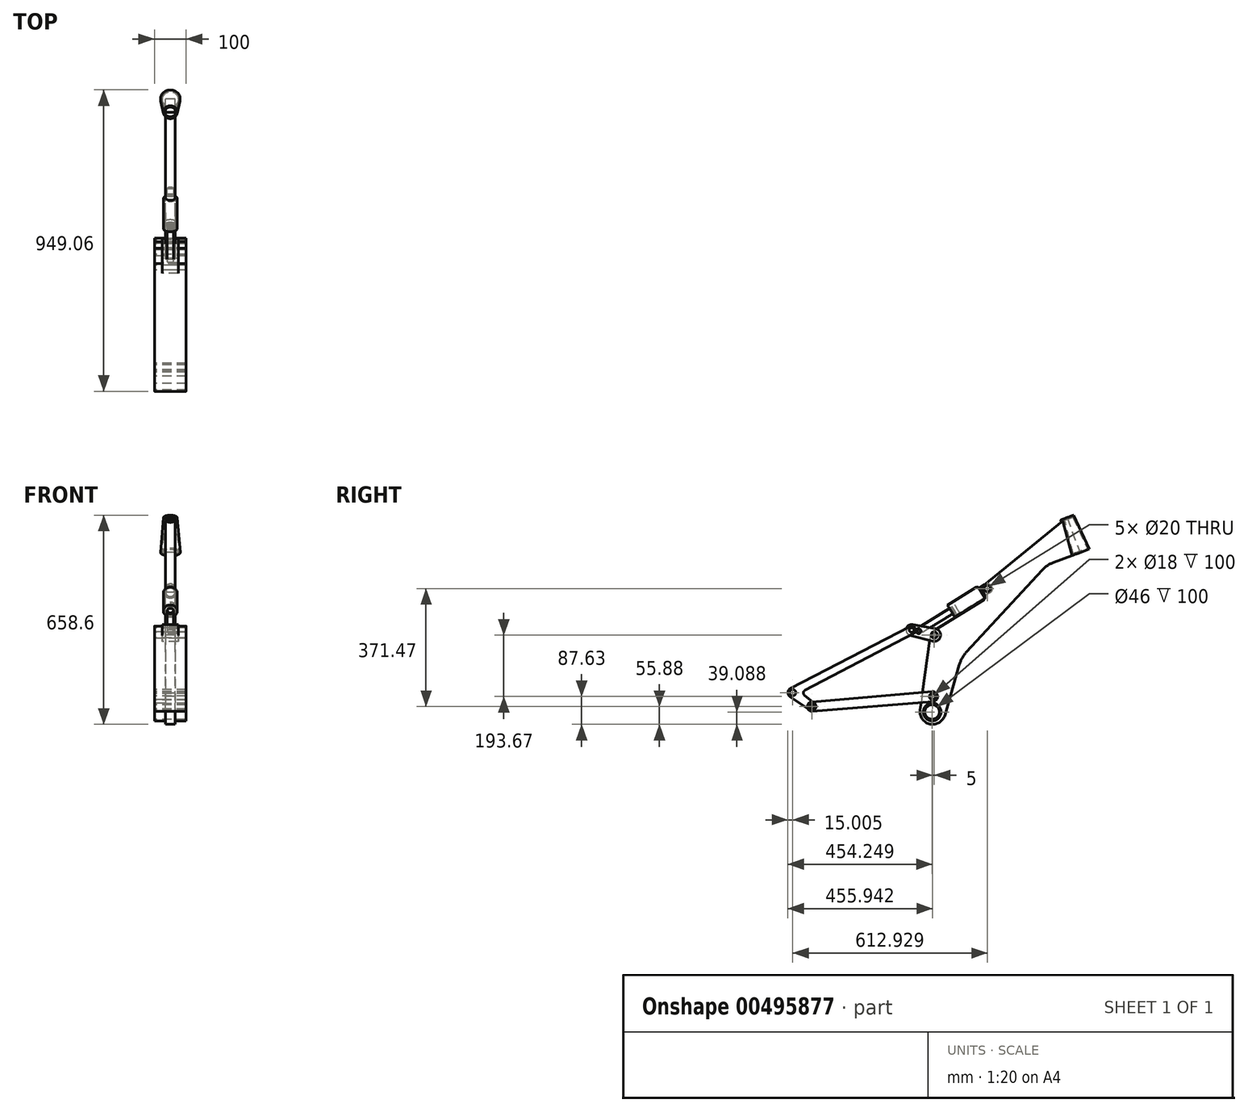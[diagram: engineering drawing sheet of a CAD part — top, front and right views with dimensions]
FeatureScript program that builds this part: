
annotation { "Feature Type Name" : "Feature", "Feature Type Description" : "" }
export const myFeature = defineFeature(function(context is Context, id is Id, definition is map)
    precondition{}
    {
        {
            var Q0;
            Q0=qCreatedBy(makeId("Right.planeOp"),FACE);
            var sketch = newSketch(context, id + "F0", { "sketchPlane" : qUnion([Q0])});
            skLineSegment(sketch, "E0", {"start": v(0, 0) * mm, "end": v(-83.68, 223.8) * mm, "construction": true});
            skLineSegment(sketch, "E1", {"start": v(-295.85, 645.65) * mm, "end": v(-16.13, -102.49) * mm, "construction": true});
            skPoint(sketch, "E2", {"position": v(-219.37, 441.1) * mm});
            skLineSegment(sketch, "E3", {"start": v(-285.85, 416.25) * mm, "end": v(-152.9, 465.96) * mm, "construction": true});
            skCircle(sketch, "E4", {"center": v(0, -8.13) * mm, "radius": 375.7 * mm, "construction": true});
            skPoint(sketch, "E5", {"position": v(-260.46, 551) * mm});
            skPoint(sketch, "E6", {"position": v(-683.46, -60) * mm});
            skPoint(sketch, "E7", {"position": v(-1124.4, 0) * mm});
            skLineSegment(sketch, "E8", {"start": v(-1124.4, 0) * mm, "end": v(0, 0) * mm, "construction": true});
            skCircle(sketch, "E9", {"center": v(-1124.4, 0) * mm, "radius": 375.7 * mm, "construction": true});
            skLineSegment(sketch, "E10", {"start": v(-683.46, -60) * mm, "end": v(-904.4, 662.68) * mm, "construction": true});
            skLineSegment(sketch, "E11", {"start": v(-260.46, 551) * mm, "end": v(-947.84, 551) * mm, "construction": true});
            skPoint(sketch, "E12", {"position": v(-870.26, 551) * mm});
            skLineSegment(sketch, "E13", {"start": v(-207.61, 570.76) * mm, "end": v(-313.3, 531.24) * mm, "construction": true});
            skPoint(sketch, "E14", {"position": v(-249.95, 522.9) * mm});
            skLineSegment(sketch, "E15", {"start": v(-683.46, -60) * mm, "end": v(-249.95, 522.9) * mm, "construction": true});
            skPoint(sketch, "E16", {"position": v(-785.79, 274.7) * mm});
            skLineSegment(sketch, "E17", {"start": v(-785.79, 274.7) * mm, "end": v(-249.95, 522.9) * mm, "construction": true});
            skPoint(sketch, "E18", {"position": v(-466.7, 231.45) * mm});
            skPoint(sketch, "E19", {"position": v(-517.87, 398.8) * mm});
            skSolve(sketch);
        }
        {
            var Q0;
            Q0=qCreatedBy(makeId("Right.planeOp"),FACE);
            var sketch = newSketch(context, id + "F1", { "sketchPlane" : qUnion([Q0])});
            skLineSegment(sketch, "E20", {"start": v(-243.73, 432) * mm, "end": v(-245.48, 436.69) * mm});
            skLineSegment(sketch, "E21", {"start": v(-275.1, 540.19) * mm, "end": v(-245.48, 436.69) * mm});
            skLineSegment(sketch, "E22", {"start": v(-275.1, 540.19) * mm, "end": v(-276.85, 544.87) * mm});
            skLineSegment(sketch, "E23", {"start": v(-276.85, 544.87) * mm, "end": v(-280.8, 543.4) * mm});
            skLineSegment(sketch, "E24", {"start": v(-280.8, 543.4) * mm, "end": v(-248.4, 430.25) * mm});
            skLineSegment(sketch, "E25", {"start": v(-248.4, 430.25) * mm, "end": v(-243.73, 432) * mm});
            skSolve(sketch);
        }
        {
            var Q0;
            Q0=qSketchRegion(id+"F1",true);
            var Q1;
            Q1=sQuery(id+"F0.wireOp",EDGE,"E1");
            revolve(context, id + "F2", {"entities" : qUnion([Q0]), "axis" : qUnion([Q1]), "revolveType" : RevolveType.FULL});
        }
        {
            var Q0;
            Q0=qCreatedBy(makeId("Right.planeOp"),FACE);
            var sketch = newSketch(context, id + "F3", { "sketchPlane" : qUnion([Q0])});
            skCircle(sketch, "E26", {"center": v(-685.15, -60.91) * mm, "radius": 23 * mm});
            skCircle(sketch, "E27", {"center": v(-685.15, -60.91) * mm, "radius": 28 * mm});
            skSolve(sketch);
        }
        {
            var Q0;
            Q0=qSketchRegion(id+"F3",true);
            extrude(context, id + "F4", {"entities" : qUnion([Q0]), "operationType" : NewBodyOperationType.ADD, "endBound" : BoundingType.SYMMETRIC, "depth" : 100 * mm});
        }
        {
            var Q0;
            Q0=qCreatedBy(makeId("Right.planeOp"),FACE);
            var sketch = newSketch(context, id + "F5", { "sketchPlane" : qUnion([Q0])});
            skPoint(sketch, "E28", {"position": v(-683.46, -12.37) * mm});
            skPoint(sketch, "E29", {"position": v(-1063.13, -44.12) * mm});
            skPoint(sketch, "E30", {"position": v(-678.46, 181.3) * mm});
            skPoint(sketch, "E31", {"position": v(-727.65, 194) * mm});
            skPoint(sketch, "E32", {"position": v(-511.47, 327.35) * mm});
            skPoint(sketch, "E33", {"position": v(-749.65, 197.18) * mm});
            skSolve(sketch);
        }
        {
            var Q0;
            Q0=qCreatedBy(makeId("Right.planeOp"),FACE);
            var sketch = newSketch(context, id + "F6", { "sketchPlane" : qUnion([Q0])});
            skArc(sketch, "E34", {"start": v(-520.93, 338.98) * mm, "mid": v(-525.9, 331.46) * mm, "end": v(-525.64, 322.45) * mm});
            skArc(sketch, "E35", {"start": v(-685, 191.95) * mm, "mid": v(-689.37, 187.4) * mm, "end": v(-690.96, 181.3) * mm});
            skLineSegment(sketch, "E36", {"start": v(-690.96, 181.3) * mm, "end": v(-723.1, -54.6) * mm});
            skLineSegment(sketch, "E37", {"start": v(-520.93, 338.98) * mm, "end": v(-260.46, 551) * mm});
            skArc(sketch, "E38", {"start": v(-723.1, -54.6) * mm, "mid": v(-691.69, -99.14) * mm, "end": v(-645, -71.01) * mm});
            skLineSegment(sketch, "E39", {"start": v(-645, -71.01) * mm, "end": v(-599.6, 87.53) * mm});
            skLineSegment(sketch, "E40", {"start": v(-576.93, 127.84) * mm, "end": v(-338.3, 386.26) * mm});
            skLineSegment(sketch, "E41", {"start": v(-303.46, 409.67) * mm, "end": v(-219.37, 441.1) * mm});
            skLineSegment(sketch, "E42", {"start": v(-260.46, 551) * mm, "end": v(-219.37, 441.1) * mm});
            skArc(sketch, "E43", {"start": v(-303.46, 409.67) * mm, "mid": v(-322.26, 400.01) * mm, "end": v(-338.3, 386.26) * mm});
            skCircle(sketch, "E44", {"center": v(-683.46, -12.28) * mm, "radius": 10 * mm});
            skArc(sketch, "E45", {"start": v(-576.93, 127.84) * mm, "mid": v(-590.62, 109.02) * mm, "end": v(-599.6, 87.53) * mm});
            skCircle(sketch, "E46", {"center": v(-678.46, 181.3) * mm, "radius": 10 * mm});
            skCircle(sketch, "E47", {"center": v(-511.47, 327.35) * mm, "radius": 10 * mm});
            skLineSegment(sketch, "E48", {"start": v(-685, 191.95) * mm, "end": v(-523.22, 291.48) * mm});
            skArc(sketch, "E49", {"start": v(-523.22, 291.48) * mm, "mid": v(-519.04, 296.64) * mm, "end": v(-519, 303.27) * mm});
            skLineSegment(sketch, "E50", {"start": v(-525.64, 322.45) * mm, "end": v(-519, 303.27) * mm});
            skCircle(sketch, "E51", {"center": v(-685.15, -60.91) * mm, "radius": 28 * mm});
            skSolve(sketch);
        }
        {
            var Q0;
            Q0 = qSketchRegion(id + "F6", true);
            extrude(context, id + "F7", {"entities" : qUnion([Q0]), "operationType" : NewBodyOperationType.ADD, "endBound" : BoundingType.SYMMETRIC, "depth" : 30 * mm});
        }
        {
            var Q0;
            Q0=qCreatedBy(makeId("Right.planeOp"),FACE);
            var sketch = newSketch(context, id + "F8", { "sketchPlane" : qUnion([Q0])});
            skCircle(sketch, "E52", {"center": v(-683.46, -12.37) * mm, "radius": 10 * mm});
            skCircle(sketch, "E53", {"center": v(-683.46, -12.37) * mm, "radius": 9 * mm});
            skSolve(sketch);
        }
        {
            var Q0;
            Q0 = qSketchRegion(id + "F8", true);
            extrude(context, id + "F9", {"entities" : qUnion([Q0]), "operationType" : NewBodyOperationType.ADD, "endBound" : BoundingType.SYMMETRIC, "depth" : 100 * mm});
        }
        {
            var Q0;
            Q0=qCreatedBy(makeId("Right.planeOp"),FACE);
            var sketch = newSketch(context, id + "F10", { "sketchPlane" : qUnion([Q0])});
            skCircle(sketch, "E54", {"center": v(-678.46, 181.3) * mm, "radius": 10 * mm});
            skCircle(sketch, "E55", {"center": v(-678.46, 181.3) * mm, "radius": 9 * mm});
            skSolve(sketch);
        }
        {
            var Q0;
            Q0 = qSketchRegion(id + "F10", true);
            extrude(context, id + "F11", {"entities" : qUnion([Q0]), "operationType" : NewBodyOperationType.ADD, "endBound" : BoundingType.SYMMETRIC, "depth" : 100 * mm});
        }
        {
            var Q0;
            Q0=qCreatedBy(makeId("Right.planeOp"),FACE);
            var sketch = newSketch(context, id + "F12", { "sketchPlane" : qUnion([Q0])});
            skCircle(sketch, "E56", {"center": v(-511.47, 327.35) * mm, "radius": 10 * mm});
            skCircle(sketch, "E57", {"center": v(-511.47, 327.35) * mm, "radius": 9 * mm});
            skSolve(sketch);
        }
        {
            var Q0;
            Q0 = qSketchRegion(id + "F12", true);
            extrude(context, id + "F13", {"entities" : qUnion([Q0]), "operationType" : NewBodyOperationType.ADD, "endBound" : BoundingType.SYMMETRIC, "depth" : 100 * mm});
        }
        {
            var Q0;
            Q0=qCreatedBy(makeId("Right.planeOp"),FACE);
            var sketch = newSketch(context, id + "F14", { "sketchPlane" : qUnion([Q0])});
            skLineSegment(sketch, "E58", {"start": v(-1064.4, -29.17) * mm, "end": v(-684.77, 3.07) * mm});
            skLineSegment(sketch, "E59", {"start": v(-1061.9, -59.07) * mm, "end": v(-682.19, -27.82) * mm});
            skArc(sketch, "E60", {"start": v(-682.19, -27.82) * mm, "mid": v(-668.01, -11.08) * mm, "end": v(-684.77, 3.07) * mm});
            skArc(sketch, "E61", {"start": v(-1064.4, -29.17) * mm, "mid": v(-1078.08, -45.37) * mm, "end": v(-1061.9, -59.07) * mm});
            skCircle(sketch, "E62", {"center": v(-683.46, -12.37) * mm, "radius": 10.5 * mm});
            skCircle(sketch, "E63", {"center": v(-1063.13, -44.12) * mm, "radius": 10 * mm});
            skSolve(sketch);
        }
        {
            var Q0;
            Q0 = qSketchRegion(id + "F14", true);
            extrude(context, id + "F15", {"entities" : qUnion([Q0]), "endBound" : BoundingType.SYMMETRIC, "depth" : 100 * mm});
        }
        {
            var Q0;
            Q0=qCreatedBy(makeId("Right.planeOp"),FACE);
            var sketch = newSketch(context, id + "F16", { "sketchPlane" : qUnion([Q0])});
            skLineSegment(sketch, "E64", {"start": v(-746.42, 214.38) * mm, "end": v(-674.78, 200.96) * mm});
            skLineSegment(sketch, "E65", {"start": v(-754.04, 180.24) * mm, "end": v(-683.48, 161.94) * mm});
            skArc(sketch, "E66", {"start": v(-746.42, 214.38) * mm, "mid": v(-766.73, 201) * mm, "end": v(-754.04, 180.24) * mm});
            skArc(sketch, "E67", {"start": v(-683.48, 161.94) * mm, "mid": v(-658.94, 176.95) * mm, "end": v(-674.78, 200.96) * mm});
            skCircle(sketch, "E68", {"center": v(-749.65, 197.18) * mm, "radius": 7.5 * mm});
            skCircle(sketch, "E69", {"center": v(-678.46, 181.3) * mm, "radius": 10 * mm});
            skCircle(sketch, "E70", {"center": v(-727.65, 194) * mm, "radius": 7.5 * mm});
            skSolve(sketch);
        }
        {
            var Q0;
            Q0 = qSketchRegion(id + "F16", true);
            extrude(context, id + "F17", {"entities" : qUnion([Q0]), "endBound" : BoundingType.SYMMETRIC, "depth" : 50 * mm});
        }
        {
            var Q0;
            Q0=qCreatedBy(makeId("Right.planeOp"),FACE);
            var sketch = newSketch(context, id + "F18", { "sketchPlane" : qUnion([Q0])});
            skLineSegment(sketch, "E71", {"start": v(-1055.2, -34.46) * mm, "end": v(-1087.68, -7.78) * mm});
            skLineSegment(sketch, "E72", {"start": v(-1070.1, -54.5) * mm, "end": v(-1132.75, -12.46) * mm});
            skLineSegment(sketch, "E73", {"start": v(-1131.3, 13.32) * mm, "end": v(-755.4, 208.28) * mm});
            skLineSegment(sketch, "E74", {"start": v(-1086.17, 6.88) * mm, "end": v(-743.85, 186.1) * mm});
            skArc(sketch, "E75", {"start": v(-743.85, 186.1) * mm, "mid": v(-738.56, 202.96) * mm, "end": v(-755.4, 208.28) * mm});
            skArc(sketch, "E76", {"start": v(-1131.3, 13.32) * mm, "mid": v(-1139.37, 0.84) * mm, "end": v(-1132.75, -12.46) * mm});
            skArc(sketch, "E77", {"start": v(-1086.17, 6.88) * mm, "mid": v(-1090.86, -0.04) * mm, "end": v(-1087.68, -7.78) * mm});
            skArc(sketch, "E78", {"start": v(-1070.1, -54.5) * mm, "mid": v(-1053.1, -51.58) * mm, "end": v(-1055.2, -34.46) * mm});
            skCircle(sketch, "E79", {"center": v(-749.65, 197.18) * mm, "radius": 7.5 * mm});
            skCircle(sketch, "E80", {"center": v(-1124.4, 0) * mm, "radius": 10 * mm});
            skCircle(sketch, "E81", {"center": v(-1063.13, -44.12) * mm, "radius": 7.5 * mm});
            skSolve(sketch);
        }
        {
            var Q0;
            Q0 = qSketchRegion(id + "F18", true);
            extrude(context, id + "F19", {"entities" : qUnion([Q0]), "endBound" : BoundingType.SYMMETRIC, "depth" : 100 * mm});
        }
        {
            var Q0;
            Q0=qCreatedBy(makeId("Right.planeOp"),FACE);
            var sketch = newSketch(context, id + "F20", { "sketchPlane" : qUnion([Q0])});
            skLineSegment(sketch, "E82", {"start": v(-818.05, 138.23) * mm, "end": v(-389.17, 402.79) * mm, "construction": true});
            skLineSegment(sketch, "E83", {"start": v(-732.9, 202.51) * mm, "end": v(-622.25, 270.76) * mm});
            skLineSegment(sketch, "E84", {"start": v(-622.25, 270.76) * mm, "end": v(-627.5, 279.27) * mm});
            skLineSegment(sketch, "E85", {"start": v(-627.5, 279.27) * mm, "end": v(-619, 284.52) * mm});
            skLineSegment(sketch, "E86", {"start": v(-619, 284.52) * mm, "end": v(-608.5, 267.5) * mm});
            skLineSegment(sketch, "E87", {"start": v(-608.5, 267.5) * mm, "end": v(-736.16, 188.75) * mm});
            skArc(sketch, "E88", {"start": v(-732.9, 202.51) * mm, "mid": v(-737.38, 196.3) * mm, "end": v(-736.16, 188.75) * mm});
            skSolve(sketch);
        }
        {
            var Q0;
            Q0 = qSketchRegion(id + "F20", true);
            var Q1;
            Q1=sQuery(id+"F20.wireOp",EDGE,"E82");
            revolve(context, id + "F21", {"entities" : qUnion([Q0]), "axis" : qUnion([Q1]), "revolveType" : RevolveType.FULL});
        }
        {
            var Q0;
            Q0=qCreatedBy(makeId("Right.planeOp"),FACE);
            var sketch = newSketch(context, id + "F22", { "sketchPlane" : qUnion([Q0])});
            skLineSegment(sketch, "E89", {"start": v(-727.65, 194) * mm, "end": v(-518.36, 323.1) * mm, "construction": true});
            skLineSegment(sketch, "E90", {"start": v(-630.76, 265.51) * mm, "end": v(-626.5, 268.14) * mm});
            skLineSegment(sketch, "E91", {"start": v(-626.5, 268.14) * mm, "end": v(-631.76, 276.65) * mm});
            skLineSegment(sketch, "E92", {"start": v(-631.76, 276.65) * mm, "end": v(-542.4, 331.77) * mm});
            skLineSegment(sketch, "E93", {"start": v(-519.34, 340.12) * mm, "end": v(-538.06, 328.57) * mm});
            skLineSegment(sketch, "E94", {"start": v(-538.06, 328.57) * mm, "end": v(-541.74, 334.52) * mm});
            skLineSegment(sketch, "E95", {"start": v(-541.74, 334.52) * mm, "end": v(-637.06, 275.72) * mm});
            skLineSegment(sketch, "E96", {"start": v(-637.06, 275.72) * mm, "end": v(-630.76, 265.51) * mm});
            skArc(sketch, "E97", {"start": v(-498.7, 335.23) * mm, "mid": v(-508, 341.95) * mm, "end": v(-519.34, 340.12) * mm});
            skLineSegment(sketch, "E98", {"start": v(-542.4, 331.77) * mm, "end": v(-531.9, 314.75) * mm});
            skLineSegment(sketch, "E99", {"start": v(-531.9, 314.75) * mm, "end": v(-498.7, 335.23) * mm});
            skSolve(sketch);
        }
        {
            var Q0;
            Q0 = qSketchRegion(id + "F22", true);
            var Q1;
            Q1=sQuery(id+"F22.wireOp",EDGE,"E89");
            revolve(context, id + "F23", {"entities" : qUnion([Q0]), "axis" : qUnion([Q1]), "revolveType" : RevolveType.FULL});
        }
        {
            var Q0;
            Q0=qCreatedBy(makeId("Right.planeOp"),FACE);
            var sketch = newSketch(context, id + "F24", { "sketchPlane" : qUnion([Q0])});
            skCircle(sketch, "E100", {"center": v(-511.47, 327.35) * mm, "radius": 10 * mm});
            skSolve(sketch);
        }
        {
            var Q0;
            Q0 = qSketchRegion(id + "F24", true);
            extrude(context, id + "F25", {"entities" : qUnion([Q0]), "operationType" : NewBodyOperationType.REMOVE, "endBound" : BoundingType.THROUGH_ALL, "oppositeDirection" : true, "depth" : 25 * mm, "hasSecondDirection" : true, "secondDirectionBound" : SecondDirectionBoundingType.THROUGH_ALL, "secondDirectionOppositeDirection" : false, "secondDirectionDepth" : 25 * mm});
        }
        {
            var Q0;
            Q0=qCreatedBy(makeId("Right.planeOp"),FACE);
            var sketch = newSketch(context, id + "F26", { "sketchPlane" : qUnion([Q0])});
            skCircle(sketch, "E101", {"center": v(-727.65, 194) * mm, "radius": 5 * mm});
            skSolve(sketch);
        }
        {
            var Q0;
            Q0 = qSketchRegion(id + "F26", true);
            extrude(context, id + "F27", {"entities" : qUnion([Q0]), "operationType" : NewBodyOperationType.REMOVE, "endBound" : BoundingType.THROUGH_ALL, "oppositeDirection" : true, "depth" : 25 * mm, "hasSecondDirection" : true, "secondDirectionBound" : SecondDirectionBoundingType.THROUGH_ALL, "secondDirectionOppositeDirection" : false, "secondDirectionDepth" : 25 * mm});
        }
        {
            var Q0;
            Q0=makeQuery(id+"F23.opRevolve","SWEPT_EDGE",EDGE,{"disambiguationData":[OSD([sQuery(id+"F22.wireOp",EDGE,"E94"),sQuery(id+"F22.wireOp",EDGE,"E95")])]});
            fillet(context, id + "F28", {"entities" : qUnion([Q0]), "radius" : 5 * mm, "tangentPropagation" : true, "allowEdgeOverflow" : false});
        }
    });
